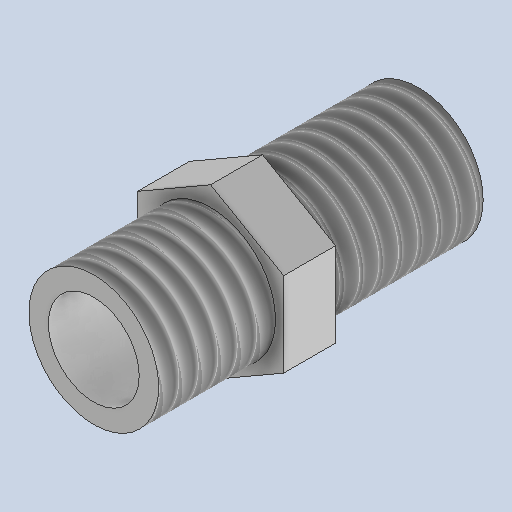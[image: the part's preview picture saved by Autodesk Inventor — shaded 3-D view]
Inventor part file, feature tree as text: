
AUTODESK INVENTOR PART (.ipt)
format: ipt  version: 2025.1 (Build 291241000, 241)  size: 183,808 bytes
history: native  units: mm
features: sketch x4, other x3
ambient origin geometry x8: Origin, YZ Plane, XZ Plane, XY Plane, X Axis, Y Axis, Z Axis, Center Point
bodies: Volumenkörper1 (feature_tree)
feature tree (7):
  other  "1154.ipt"
  other  "Volumenkörper1::1154.ipt"
  other  "TaggingFeature1"
  sketch  "Skizze1"  dims[d0=10.0mm]
  sketch  "Skizze2"
  sketch  "Skizze3"
  sketch  "Skizze4"
